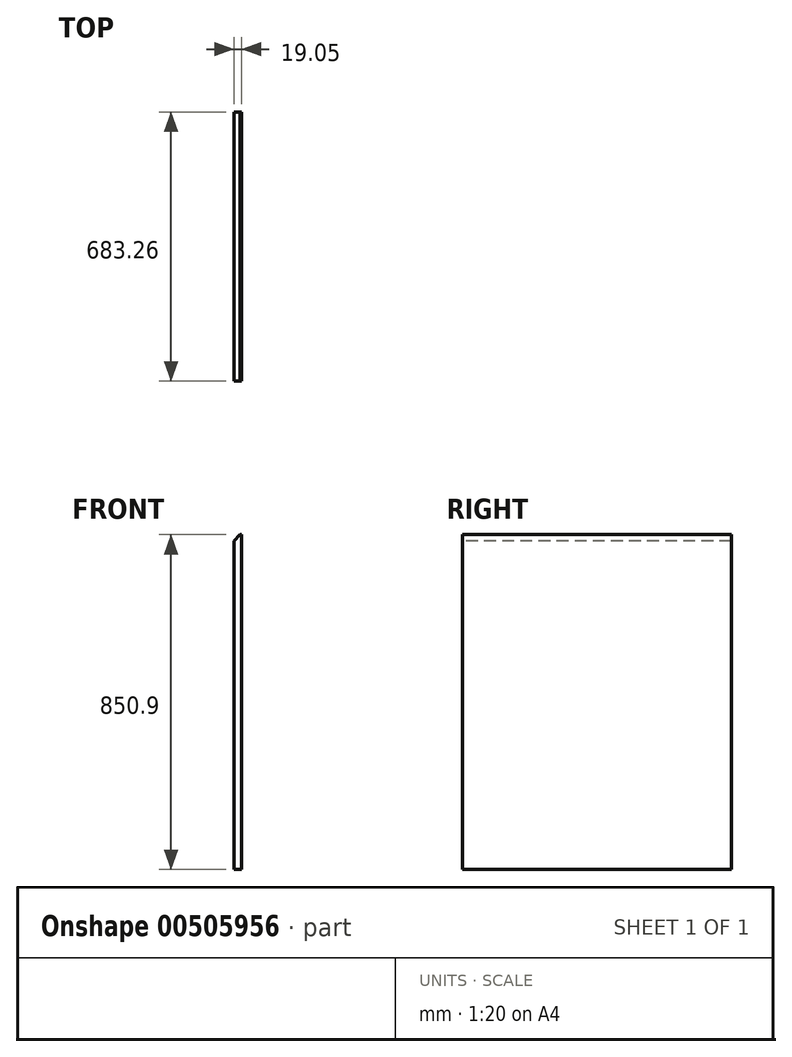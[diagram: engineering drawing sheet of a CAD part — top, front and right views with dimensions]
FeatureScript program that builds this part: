
annotation { "Feature Type Name" : "Feature", "Feature Type Description" : "" }
export const myFeature = defineFeature(function(context is Context, id is Id, definition is map)
    precondition{}
    {
        {
            var Q0;
            Q0=qCreatedBy(makeId("Right.planeOp"),FACE);
            var sketch = newSketch(context, id + "F0", { "sketchPlane" : qUnion([Q0])});
            skLineSegment(sketch, "E0.bottom", {"start": v(-340.15, 528.15) * mm, "end": v(343.1, 528.15) * mm});
            skLineSegment(sketch, "E0.top", {"start": v(-340.15, -322.75) * mm, "end": v(343.1, -322.75) * mm});
            skLineSegment(sketch, "E0.left", {"start": v(-340.15, 528.15) * mm, "end": v(-340.15, -322.75) * mm});
            skLineSegment(sketch, "E0.right", {"start": v(343.1, 528.15) * mm, "end": v(343.1, -322.75) * mm});
            skSolve(sketch);
        }
        {
            var Q0;
            Q0=makeQuery(id+"F0.imprint","IMPRINT",FACE,{"disambiguationData":[TD([[makeQuery(id+"F0.imprint","IMPRINT",EDGE,{"derivedFrom":sQuery(id+"F0.wireOp",EDGE,"E0.bottom")}),-1.0]])]});
            extrude(context, id + "F1", {"entities" : qUnion([Q0]), "depth" : 19.05 * mm, "offsetDistance" : 25.4 * mm});
        }
        {
            var Q0;
            Q0=makeQuery(id+"F1.opExtrude","SWEPT_FACE",FACE,{"disambiguationData":[OSD([sQuery(id+"F0.wireOp",EDGE,"E0.left")])]});
            var sketch = newSketch(context, id + "F2", { "sketchPlane" : qUnion([Q0])});
            skLineSegment(sketch, "E1", {"start": v(15.77, 528.15) * mm, "end": v(0, 512.38) * mm});
            skSolve(sketch);
        }
        {
            var Q0;
            {var subQ0=sQuery(id+"F2.wireOp",EDGE,"E1");Q0=makeQuery(id+"F2.imprint","IMPRINT",FACE,{"disambiguationData":[TD([[makeQuery(id+"F2.imprint","IMPRINT",EDGE,{"derivedFrom":subQ0}),-1.0]])]});}
            extrude(context, id + "F3", {"entities" : qUnion([Q0]), "operationType" : NewBodyOperationType.REMOVE, "depth" : -683.26 * mm, "offsetDistance" : 25.4 * mm});
        }
    });
